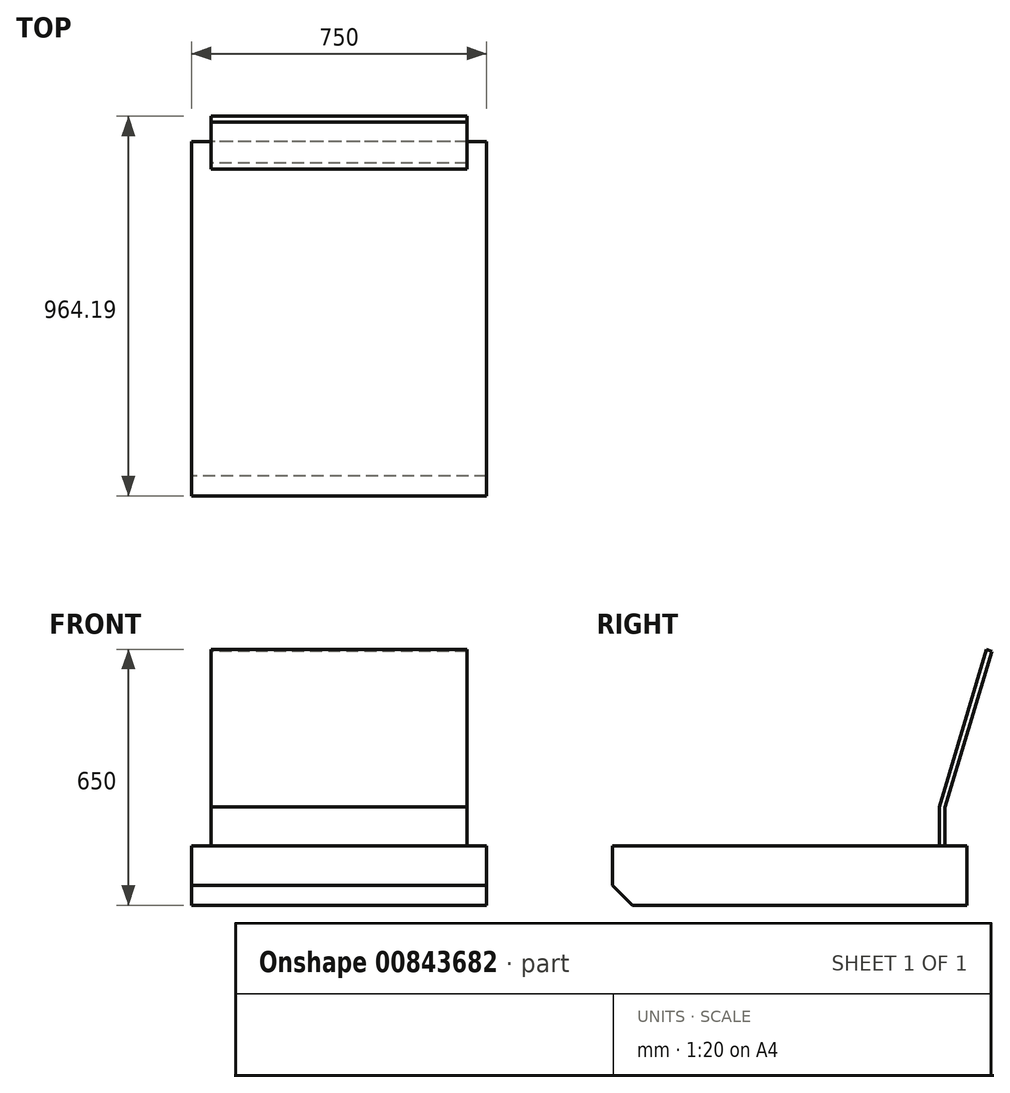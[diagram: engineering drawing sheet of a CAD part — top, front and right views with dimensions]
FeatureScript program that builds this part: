
annotation { "Feature Type Name" : "Feature", "Feature Type Description" : "" }
export const myFeature = defineFeature(function(context is Context, id is Id, definition is map)
    precondition{}
    {
        {
            var Q0;
            Q0=qCreatedBy(makeId("Right.planeOp"),FACE);
            var sketch = newSketch(context, id + "F0", { "sketchPlane" : qUnion([Q0])});
            skLineSegment(sketch, "E0.bottom", {"start": v(450, 75) * mm, "end": v(-450, 75) * mm});
            skLineSegment(sketch, "E0.top", {"start": v(450, -75) * mm, "end": v(-450, -75) * mm});
            skLineSegment(sketch, "E0.left", {"start": v(450, 75) * mm, "end": v(450, -75) * mm});
            skLineSegment(sketch, "E0.right", {"start": v(-450, 75) * mm, "end": v(-450, -75) * mm});
            skPoint(sketch, "E0.middle", {"position": v(0, 0) * mm});
            skSolve(sketch);
        }
        {
            var Q0;
            Q0=makeQuery(id+"F0.imprint","IMPRINT",FACE,{"disambiguationData":[TD([[makeQuery(id+"F0.imprint","IMPRINT",EDGE,{"derivedFrom":sQuery(id+"F0.wireOp",EDGE,"E0.bottom")}),1.0]])]});
            extrude(context, id + "F1", {"entities" : qUnion([Q0]), "endBound" : BoundingType.SYMMETRIC, "depth" : 750 * mm, "offsetDistance" : 25 * mm});
        }
        {
            var Q0;
            Q0=makeQuery(id+"F1.opExtrude","SWEPT_EDGE",EDGE,{"disambiguationData":[OSD([sQuery(id+"F0.wireOp",EDGE,"E0.top"),sQuery(id+"F0.wireOp",EDGE,"E0.right")])]});
            chamfer(context, id + "F2", {"entities" : qUnion([Q0]), "width" : 50 * mm, "tangentPropagation" : true});
        }
        {
            var Q0;
            Q0=qCreatedBy(makeId("Right.planeOp"),FACE);
            var sketch = newSketch(context, id + "F3", { "sketchPlane" : qUnion([Q0])});
            skLineSegment(sketch, "E1", {"start": v(380, 75) * mm, "end": v(380, 175) * mm});
            skLineSegment(sketch, "E2", {"start": v(380, 175) * mm, "end": v(500, 575) * mm});
            skLineSegment(sketch, "E3.0", {"start": v(395, 172.8) * mm, "end": v(514.2, 570.1) * mm});
            skLineSegment(sketch, "E3.1", {"start": v(395, 75) * mm, "end": v(395, 172.8) * mm});
            skLineSegment(sketch, "E4", {"start": v(380, 75) * mm, "end": v(395, 75) * mm});
            skLineSegment(sketch, "E5", {"start": v(500, 575) * mm, "end": v(514.2, 570.1) * mm});
            skSolve(sketch);
        }
        {
            var Q0;
            Q0=makeQuery(id+"F3.imprint","IMPRINT",FACE,{"disambiguationData":[TD([[makeQuery(id+"F3.imprint","IMPRINT",EDGE,{"derivedFrom":sQuery(id+"F3.wireOp",EDGE,"E1")}),-1.0]])]});
            extrude(context, id + "F4", {"entities" : qUnion([Q0]), "operationType" : NewBodyOperationType.ADD, "endBound" : BoundingType.SYMMETRIC, "depth" : 650 * mm, "offsetDistance" : 25 * mm});
        }
    });
